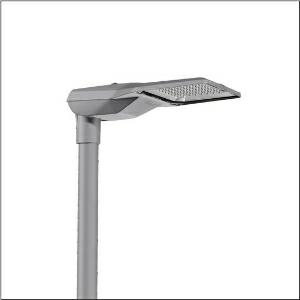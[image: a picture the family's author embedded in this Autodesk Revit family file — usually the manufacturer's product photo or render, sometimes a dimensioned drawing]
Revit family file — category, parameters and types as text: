
# Revit family: streetlight_sl_21_iq_midi___st1_0a_5xe3d31v08mb_ff90
name_source: partatom
category: Lighting Fixtures
units: mm (PartAtom-declared; Revit-internal decimal feet)

## family parameters
Cut with Voids When Loaded = No
Host = Face
Light Source = No
Part Type = Normal
Room Calculation Point = No
Round Connector Dimension = Use Diameter
Shared = No

## types (1)
- --- (1 x LED, 18340 lm, 129.3 W, 3000K)
    Apparent Load = 129 VA
    CIE Flux Codes = 37 72 97 100 100
    Color Rendering = 70
    Color Temperature = 3000K
    Default Elevation = 1800 mm
    Description = Streetlight SL 21 iQ midi, mast luminaire, primary light control with lens, of PMMA, primary optical cover: cover, of toughened safety glass, transparent, light distribution: ST1.0a, light emission: direct distribution, primary light characteristic: asymmetric, installation type: post-top, side-entry, LED, High Power LED, rated luminous flux: 18.340lm, luminous efficacy: 142lm/W, light colour: 730, colour temperature: 3000K, control gear: iQ-Street Remote, D4i with power reduction, control: pre-setting: logarithmic dimming characteristic, Street-Remote, Auto-Match, Temp-Guard, Lumen-Switch, Night-Set, Smart-Wire, Light-Fading, Desk-Remote (wireless, voltage-free reading and setting of iQ features in the workshop via application-optimized NFC function/RFID function), optimised constant luminous flux control (CLO 2.0), mains connection: 230..240V, AC, 50/60Hz, start of lifetime: 129W, end of service life: 142W, reduction: 56W, luminaire housing, of diecast aluminium, powder-coated, Siteco® metallic grey (DB 702S), corrosivity category C5 mid according to DIN EN ISO 12944, please order mast flange separately, inclination adjustable: 0°, 5°, 10°, 15°, sealing non-destructively replaceable, multi-level sealing system, length: 644mm, width: 335mm, height: 110mm, mast flange for spigot size: 42mm (side-entry): 5XC10008XM4, 60/48mm (side-entry/post-top): 5XC10108XM2, 76/60mm (side-entry/post-top): 5XC10108XM1, mounting height: 4..8m, Smart Interface above, protection rating (complete): IP66, insulation class (complete): insulation class II (safety insulation), certification: CE, ENEC, ENEC+, VDE, impact resistance: IK10, permissible operating ambient temperature for outdoor applications: -40..+50°C, standard-compliant lighting for roads and squares, packaging unit: 1 piece

Light Distribution: ST1.0a
    Height = 111 mm
    Lamp = 1 x LED
    Lamp Light Flux = 18340 lm
    Lamp Power = 129.3 W
    Lamp count = 1
    Length = 644 mm
    Luminous efficacy = 142 lm/W
    Manufacturer = Siteco
    ModVariant = No
    Model = 5XE3D31V08MB
    Number of Poles = 1
    OnlyDefault = Yes
    Power Factor = 1
    Product Name = Streetlight SL 21 iQ midi | ST1.0a
    Product group = mast luminaire | pylon top
    ProductGroupID = 6100
    Protection Class = Protection class II
    Protection Degree = IP 66
    RLX_Detail_Level = 1
    RLX_Emergency_Light_Flux = 0 lm
    RLX_Emergency_Type = 0
    RLX_Emergency_Type_DB = No
    RlxData = <blob elided: 27125 chars, md5=dbeba91e>
    Socket = socket
    Standby Power = 0 W
    System Light Flux = 18340 lm
    System Power = 129 W
    Type Comments = factory setting: luminous flux: 100 % | dim-lin: 254 | 672 mA
    Type Image = l_1004302.jpg
    URL = http://relux.com
    VarID = @adj_114644
    Voltage = 0 V
    Weight = 0.00 kg
    Width = 336 mm

## geometry (parser evidence)
native form markers: Blend x4, Sweep x11
no freeform markers — native parametric forms only
